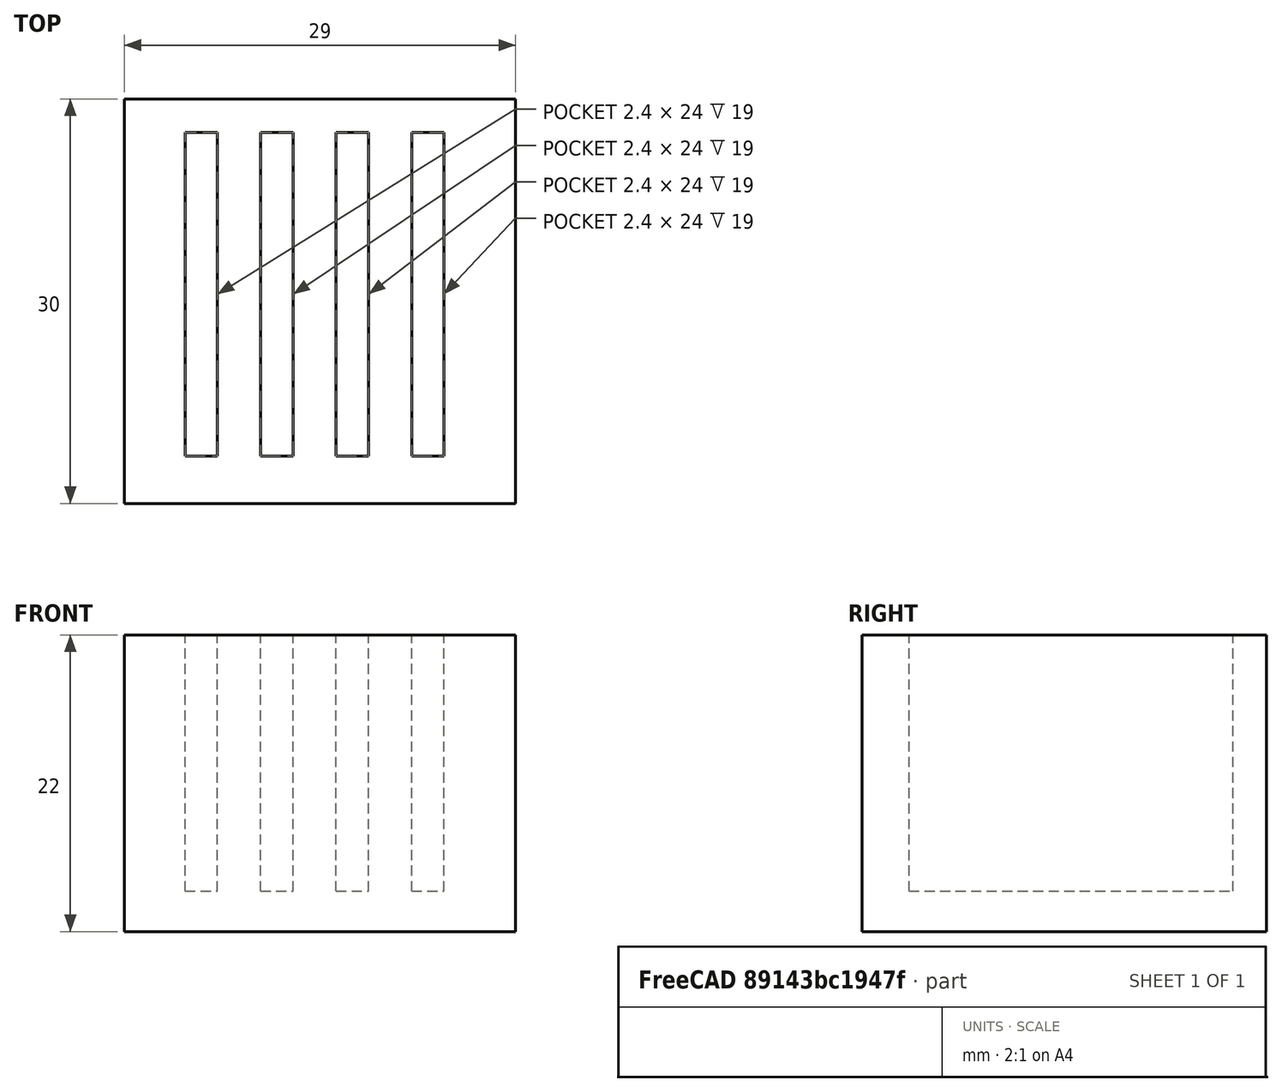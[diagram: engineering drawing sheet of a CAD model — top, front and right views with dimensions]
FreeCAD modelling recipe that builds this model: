
FCSTD DOCUMENT  (FreeCAD 0.21R33694 (Git))
Label: OJT1_T08R07_porta_caretes_fulls
License: All rights reserved
LicenseURL: http://en.wikipedia.org/wiki/All_rights_reserved
objects: Part::Box×5, Part::MultiFuse×1, Part::Cut×1
note: 7 computed .brp shape members not serialized (recipe doc carries the construction recipe); baked Part::Feature solids carry a one-line shape summary decoded from their .brp

FEATURE [Part::Box] Box  label="ranura1"
  AttacherType = Attacher::AttachEngine3D
  Height = 22
  Length = 2.4
  Width = 24
FEATURE [Part::Box] Box001  label="ranura2"
  AttacherType = Attacher::AttachEngine3D
  Height = 22
  Length = 2.4
  Placement = pos=(5.6,0,0) rot=(0,0,1;0rad)
  Width = 24
FEATURE [Part::Box] Box002  label="ranura3"
  AttacherType = Attacher::AttachEngine3D
  Height = 22
  Length = 2.4
  Placement = pos=(11.2,0,0) rot=(0,0,1;0rad)
  Width = 24
FEATURE [Part::Box] Box003  label="ranura4"
  AttacherType = Attacher::AttachEngine3D
  Height = 22
  Length = 2.4
  Placement = pos=(16.8,0,0) rot=(0,0,1;0rad)
  Width = 24
FEATURE [Part::MultiFuse] Fusion  label="ranuras"
  Placement = pos=(0,0,3) rot=(0,0,1;0rad)
  Refine = true
  Shapes = -> [Box,Box001,Box002,Box003]
FEATURE [Part::Box] Box004  label="base"
  AttacherType = Attacher::AttachEngine3D
  Height = 22
  Length = 29
  Placement = pos=(-4.5,-3.5,0) rot=(0,0,1;0rad)
  Width = 30
FEATURE [Part::Cut] Cut
  Base = -> Box004
  Refine = true
  Tool = -> Fusion
